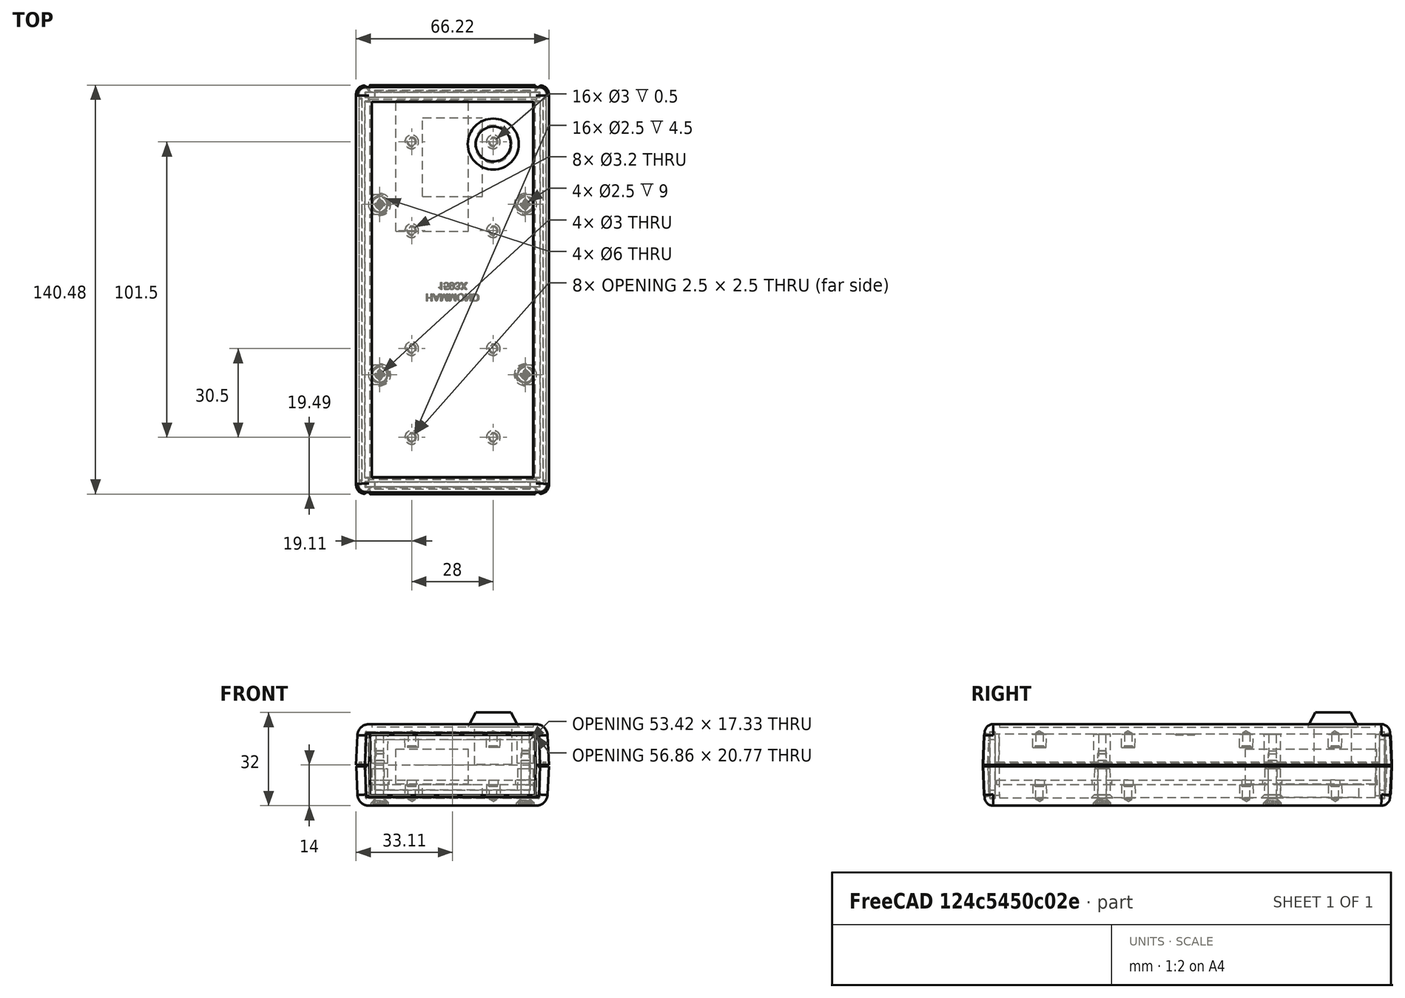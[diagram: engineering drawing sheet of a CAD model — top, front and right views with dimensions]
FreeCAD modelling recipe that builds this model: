
FCSTD DOCUMENT  (FreeCAD 0.16R)
Label: box
License: All rights reserved
LicenseURL: http://en.wikipedia.org/wiki/All_rights_reserved
objects: Part::Feature×11, Part::Box×2, Part::Cylinder×1, Part::Cone×1, Part::MultiFuse×1
note: 16 computed .brp shape members not serialized (recipe doc carries the construction recipe); baked Part::Feature solids carry a one-line shape summary decoded from their .brp

FEATURE [Part::Feature] Part__Feature  label="1593X Bot"
  Placement = pos=(0,0,-14) rot=(0,0,1;3.14159rad)
  shape: bbox 66.2 x 140.2 x 14.82 mm, 162 faces (baked)
FEATURE [Part::Feature] Part__Feature001  label="1593X Top"
  Placement = pos=(0,0,14) rot=(1,0,0;3.14159rad)
  shape: bbox 66.24 x 140.2 x 311.5 mm, 334 faces (baked)
FEATURE [Part::Feature] Part__Feature002  label="1593K-L-P-Q-X-Y Flat endplate"
  Placement = pos=(0,66.9032,0) rot=(-1,0,0;1.5708rad)
  shape: bbox 60 x 1.7 x 22.7 mm, 10 faces (baked)
FEATURE [Part::Feature] Part__Feature003  label="1593K-L-P-Q-X-Y Flat endplate001"
  Placement = pos=(0,-66.9032,0) rot=(-1,0,0;1.5708rad)
  shape: bbox 60 x 1.7 x 22.7 mm, 10 faces (baked)
FEATURE [Part::Feature] Part__Feature004  label="1593K-L-P-Q-X-Y Contoured Endplate"
  Placement = pos=(0,66.9032,0) rot=(-1,0,0;1.5708rad)
  shape: bbox 59.51 x 4.203 x 22.63 mm, 31 faces (baked)
FEATURE [Part::Feature] Part__Feature005  label="1593K-L-P-Q-X-Y Contoured Endplate001"
  Placement = pos=(0,-66.9032,0) rot=(1,0,0;1.5708rad)
  shape: bbox 59.51 x 4.203 x 22.63 mm, 31 faces (baked)
FEATURE [Part::Feature] Part__Feature006  label="1593X PCB"
  Placement = pos=(-14,-20.5,-6.8) rot=(1,0,0;3.14159rad)
  shape: bbox 56.61 x 130.7 x 1.6 mm, 30 faces (baked)
FEATURE [Part::Feature] Part__Feature007  label="SC549 (screw #4X 3_4' OH)"
  Placement = pos=(25,-29.25,-11.7547) rot=(-1,0,0;1.5708rad)
  shape: bbox 5.525 x 5.525 x 18.81 mm, 28 faces (baked)
FEATURE [Part::Feature] Part__Feature008  label="SC549 (screw #4X 3_4' OH)001"
  Placement = pos=(-25,-29.25,-11.9628) rot=(-1,0,0;1.5708rad)
  shape: bbox 5.525 x 5.525 x 18.81 mm, 28 faces (baked)
FEATURE [Part::Feature] Part__Feature009  label="SC549 (screw #4X 3_4' OH)002"
  Placement = pos=(-25,29.25,-11.9628) rot=(-1,0,0;1.5708rad)
  shape: bbox 5.525 x 5.525 x 18.81 mm, 28 faces (baked)
FEATURE [Part::Feature] Part__Feature010  label="SC549 (screw #4X 3_4' OH)003"
  Placement = pos=(25,29.25,-11.9628) rot=(-1,0,0;1.5708rad)
  shape: bbox 5.525 x 5.525 x 18.81 mm, 28 faces (baked)
FEATURE [Part::Box] Box  label="Rangefinder"
  Height = 12
  Length = 25
  Placement = pos=(-19.5,20,-6.5) rot=(0,0,1;0rad)
  Width = 45
FEATURE [Part::Box] Box001  label="Battery"
  Height = 4.3
  Length = 20.5
  Placement = pos=(-10.25,32,-11) rot=(0,0,1;0rad)
  Width = 27
FEATURE [Part::Cylinder] Cylinder
  Angle = 360
  Height = 12.9
  Placement = pos=(0,0,-12.9) rot=(0,0,1;0rad)
  Radius = 6.45
FEATURE [Part::Cone] Cone
  Angle = 360
  Height = 5
  Radius1 = 8.75
  Radius2 = 6
FEATURE [Part::MultiFuse] Fusion
  Placement = pos=(14,50,13) rot=(0,0,1;0rad)
  Shapes = -> [Cylinder,Cone]
